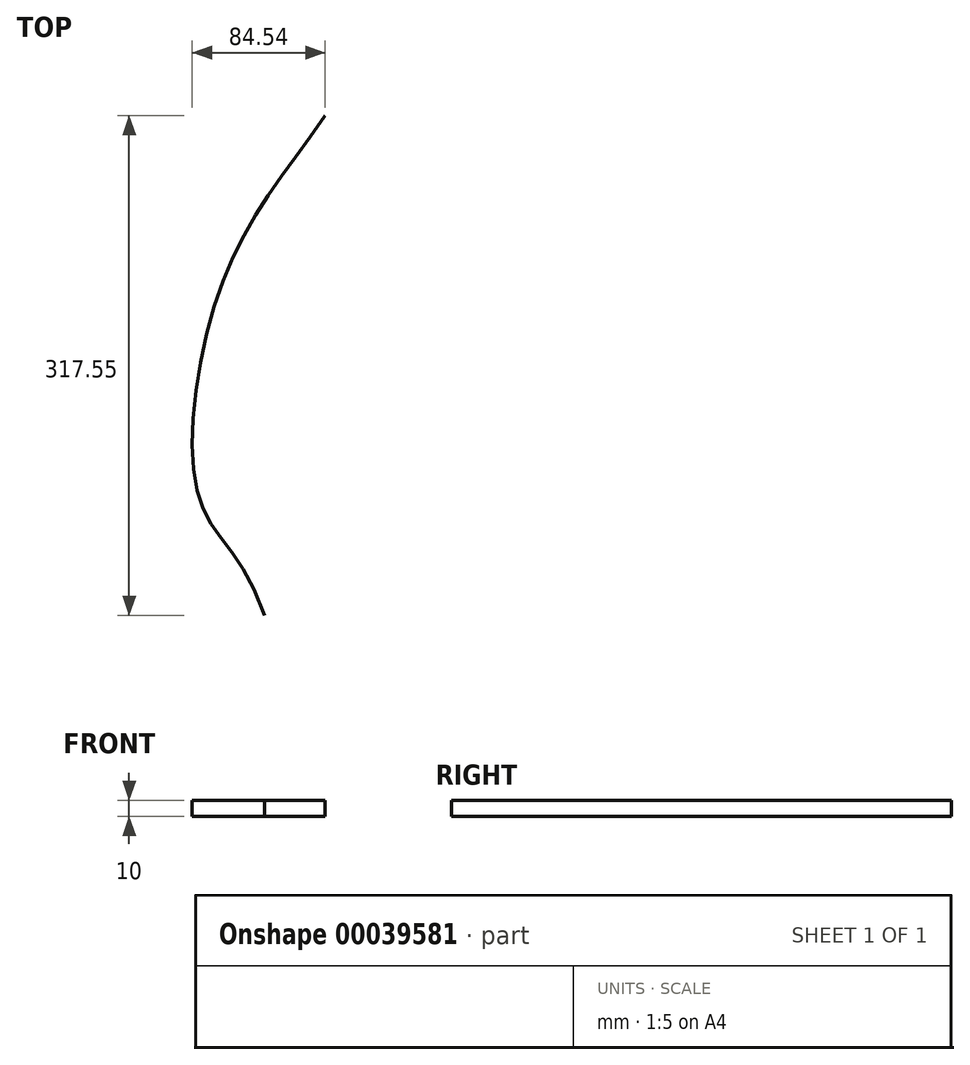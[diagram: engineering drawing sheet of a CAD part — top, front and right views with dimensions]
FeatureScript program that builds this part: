
annotation { "Feature Type Name" : "Feature", "Feature Type Description" : "" }
export const myFeature = defineFeature(function(context is Context, id is Id, definition is map)
    precondition{}
    {
        {
            var Q0;
            Q0=qCreatedBy(makeId("Top.planeOp"),FACE);
            var sketch = newSketch(context, id + "F0", { "sketchPlane" : qUnion([Q0])});
            skFitSpline(sketch, "E0", {"points": [v(-163.94, 84.3) * mm, v(-205.5, 159.09) * mm, v(-189.64, 298.47) * mm, v(-125.3, 401.85) * mm], "startDerivative": vector(-142.9, 427.89) * mm, "endDerivative": vector(223.79, 322.01) * mm});
            skSolve(sketch);
        }
        {
            var Q0;
            Q0=sQuery(id+"F0.wireOp",EDGE,"E0");
            extrude(context, id + "F1", {"bodyType" : ToolBodyType.SURFACE, "surfaceEntities" : qUnion([Q0]), "depth" : 10 * mm});
        }
    });
